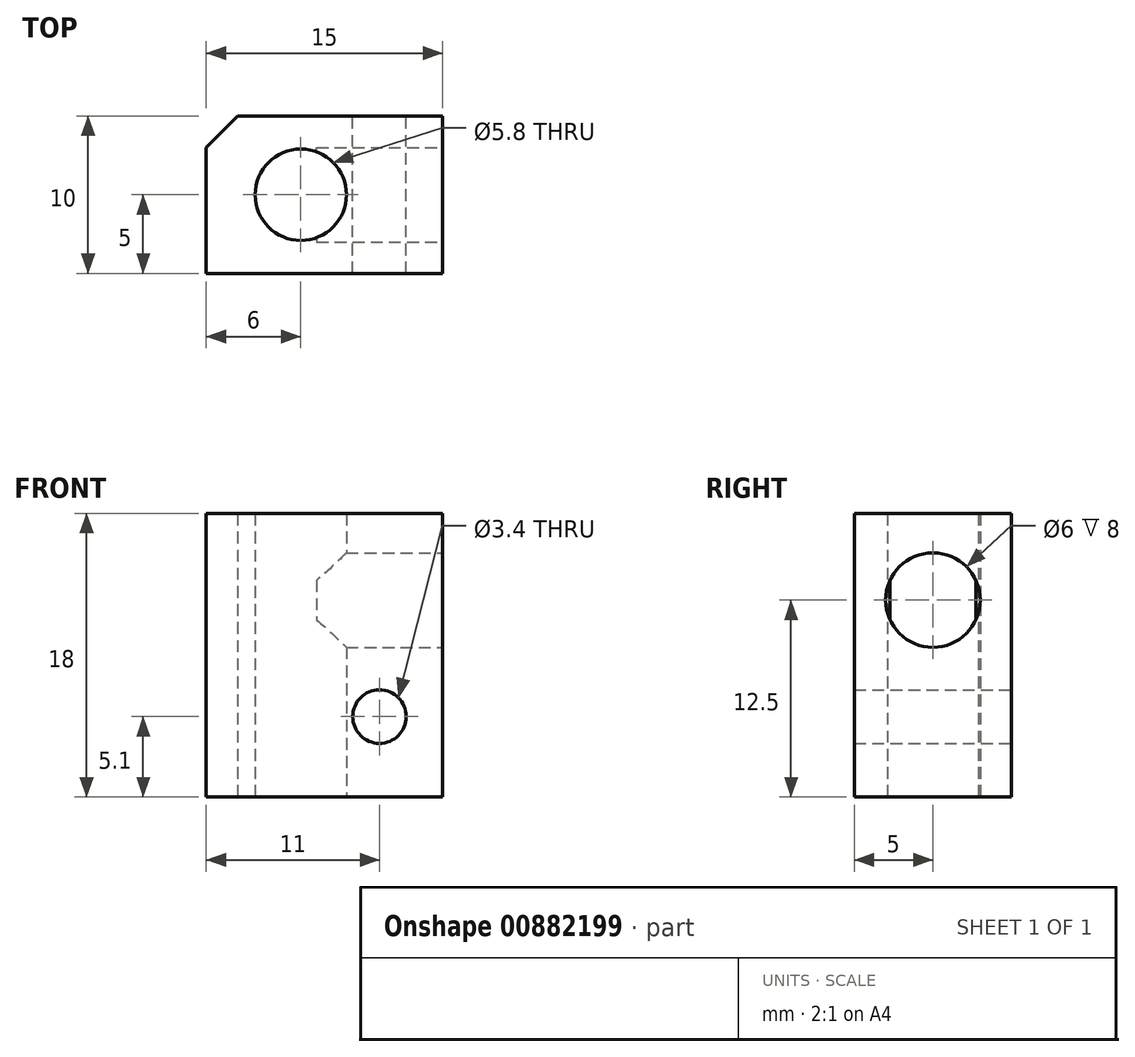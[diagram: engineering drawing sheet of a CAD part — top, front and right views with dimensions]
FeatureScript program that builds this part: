
annotation { "Feature Type Name" : "Feature", "Feature Type Description" : "" }
export const myFeature = defineFeature(function(context is Context, id is Id, definition is map)
    precondition{}
    {
        {
            var Q0;
            Q0=qCreatedBy(makeId("Top.planeOp"),FACE);
            var sketch = newSketch(context, id + "F0", { "sketchPlane" : qUnion([Q0])});
            skLineSegment(sketch, "E0.bottom", {"start": v(7.5, 5) * mm, "end": v(-5.5, 5) * mm});
            skLineSegment(sketch, "E0.top", {"start": v(7.5, -5) * mm, "end": v(-7.5, -5) * mm});
            skLineSegment(sketch, "E0.left", {"start": v(7.5, 5) * mm, "end": v(7.5, -5) * mm});
            skLineSegment(sketch, "E0.right", {"start": v(-7.5, 3) * mm, "end": v(-7.5, -5) * mm});
            skPoint(sketch, "E0.middle", {"position": v(0, 0) * mm});
            skLineSegment(sketch, "E1", {"start": v(-7.5, 3) * mm, "end": v(-5.5, 5) * mm});
            skPoint(sketch, "E2.orphan", {"position": v(-7.5, 5) * mm});
            skCircle(sketch, "E3", {"center": v(-1.5, 0) * mm, "radius": 2.5 * mm, "construction": true});
            skCircle(sketch, "E4", {"center": v(-1.5, 0) * mm, "radius": 2.9 * mm});
            skSolve(sketch);
        }
        {
            var Q0;
            Q0=makeQuery(id+"F0.imprint","IMPRINT",FACE,{"disambiguationData":[TD([[makeQuery(id+"F0.imprint","IMPRINT",EDGE,{"derivedFrom":sQuery(id+"F0.wireOp",EDGE,"E0.bottom")}),1.0]])]});
            extrude(context, id + "F1", {"entities" : qUnion([Q0]), "depth" : 18 * mm, "offsetDistance" : 25 * mm});
        }
        {
            var Q0;
            Q0=makeQuery(id+"F1.opExtrude","SWEPT_FACE",FACE,{"disambiguationData":[OSD([sQuery(id+"F0.wireOp",EDGE,"E0.left")])]});
            var sketch = newSketch(context, id + "F2", { "sketchPlane" : qUnion([Q0])});
            skCircle(sketch, "E5", {"center": v(0, 12.5) * mm, "radius": 3 * mm});
            skPoint(sketch, "E5.centerSnap0", {"position": v(0, 18) * mm});
            skSolve(sketch);
        }
        {
            var Q0;
            Q0=makeQuery(id+"F1.opExtrude","SWEPT_FACE",FACE,{"disambiguationData":[OSD([sQuery(id+"F0.wireOp",EDGE,"E0.bottom")])]});
            var sketch = newSketch(context, id + "F3", { "sketchPlane" : qUnion([Q0])});
            skCircle(sketch, "E6", {"center": v(-3.5, 5.1) * mm, "radius": 1.7 * mm});
            skSolve(sketch);
        }
        {
            var Q0;
            Q0=makeQuery(id+"F3.imprint","IMPRINT",FACE,{"disambiguationData":[TD([[makeQuery(id+"F3.imprint","IMPRINT",EDGE,{"derivedFrom":sQuery(id+"F3.wireOp",EDGE,"E6")}),1.0]])]});
            extrude(context, id + "F4", {"entities" : qUnion([Q0]), "operationType" : NewBodyOperationType.REMOVE, "endBound" : BoundingType.THROUGH_ALL, "oppositeDirection" : true, "depth" : 25 * mm, "offsetDistance" : 25 * mm});
        }
        {
            var Q0;
            Q0=makeQuery(id+"F2.imprint","IMPRINT",FACE,{"disambiguationData":[TD([[makeQuery(id+"F2.imprint","IMPRINT",EDGE,{"derivedFrom":sQuery(id+"F2.wireOp",EDGE,"E5")}),1.0]])]});
            extrude(context, id + "F5", {"entities" : qUnion([Q0]), "operationType" : NewBodyOperationType.REMOVE, "oppositeDirection" : true, "depth" : 8 * mm, "offsetDistance" : 25 * mm});
        }
    });
